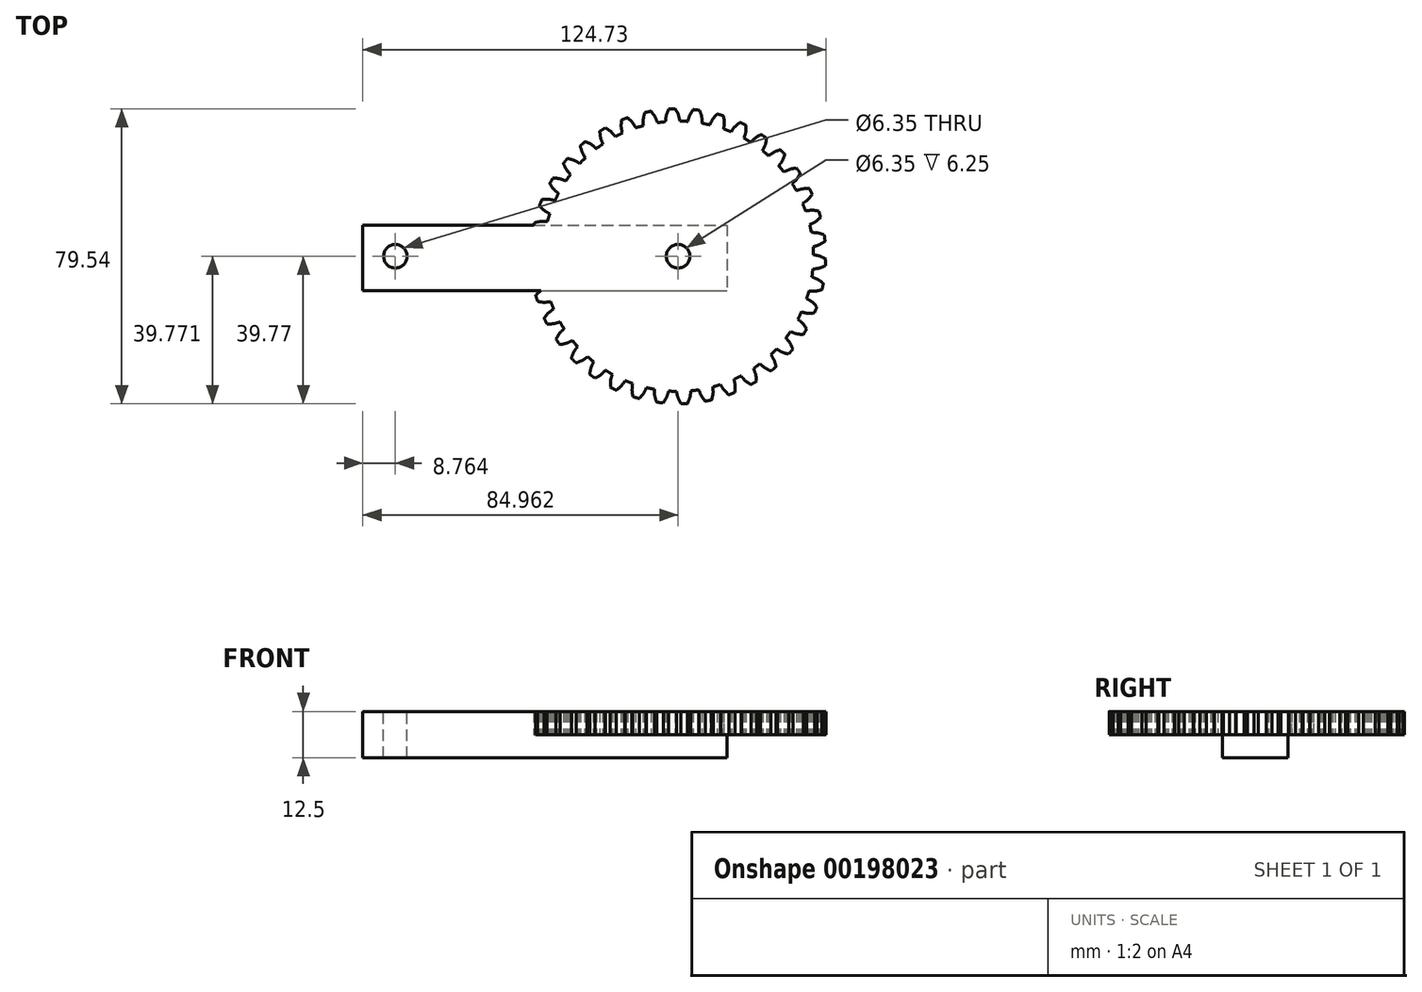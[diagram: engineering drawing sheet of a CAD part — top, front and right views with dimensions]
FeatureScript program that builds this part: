
annotation { "Feature Type Name" : "Feature", "Feature Type Description" : "" }
export const myFeature = defineFeature(function(context is Context, id is Id, definition is map)
    precondition{}
    {
        {
            var Q0;
            Q0=qCreatedBy(makeId("Top.planeOp"),FACE);
            var sketch = newSketch(context, id + "F0", { "sketchPlane" : qUnion([Q0])});
            skCircle(sketch, "E0", {"center": v(0, 0) * mm, "radius": 38.1 * mm, "construction": true});
            skLineSegment(sketch, "E1", {"start": v(0, 0) * mm, "end": v(0, 54.47) * mm, "construction": true});
            skLineSegment(sketch, "E2", {"start": v(-40.8, 38.1) * mm, "end": v(45.04, 38.1) * mm, "construction": true});
            skLineSegment(sketch, "E3", {"start": v(-12.24, 33.64) * mm, "end": v(18.8, 44.94) * mm, "construction": true});
            skLineSegment(sketch, "E4", {"start": v(0, 0) * mm, "end": v(-12.24, 33.64) * mm, "construction": true});
            skCircle(sketch, "E5", {"center": v(0, 0) * mm, "radius": 35.8 * mm, "construction": true});
            skPoint(sketch, "E6", {"position": v(-12.24, 33.64) * mm});
            skPoint(sketch, "E7", {"position": v(0, 38.1) * mm});
            skPoint(sketch, "E8", {"position": v(-16.8, 31.61) * mm});
            skLineSegment(sketch, "E9", {"start": v(-16.8, 31.61) * mm, "end": v(-0.9, 40.1) * mm, "construction": true});
            skArc(sketch, "E10", {"start": v(-7.44, 35.02) * mm, "mid": v(-9.87, 34.42) * mm, "end": v(-12.24, 33.64) * mm});
            skArc(sketch, "E11", {"start": v(-12.24, 33.64) * mm, "mid": v(-14.56, 32.7) * mm, "end": v(-16.8, 31.61) * mm});
            skLineSegment(sketch, "E12", {"start": v(-7.44, 35.02) * mm, "end": v(0.41, 36.69) * mm, "construction": true});
            skLineSegment(sketch, "E13", {"start": v(0, 38.1) * mm, "end": v(0, 0) * mm, "construction": true});
            skLineSegment(sketch, "E14", {"start": v(0.41, 36.69) * mm, "end": v(0.43, 36.44) * mm});
            skArc(sketch, "E15.trimOffspring", {"start": v(0, 36.44) * mm, "mid": v(0, 36.44) * mm, "end": v(0, 36.44) * mm});
            skLineSegment(sketch, "E16", {"start": v(0, 0) * mm, "end": v(-1.9, 46.38) * mm, "construction": true});
            skLineSegment(sketch, "E17.0.MirrorCS", {"start": v(5.36, 0.33) * mm, "end": v(1.52, 46.59) * mm, "construction": true});
            skLineSegment(sketch, "E18.0.MirrorCS", {"start": v(-3.43, 36.53) * mm, "end": v(-3.42, 36.28) * mm});
            skArc(sketch, "E19.converted", {"start": v(-3.42, 36.28) * mm, "mid": v(1.5, -36.41) * mm, "end": v(0.43, 36.44) * mm});
            skLineSegment(sketch, "E20", {"start": v(-3.42, 36.28) * mm, "end": v(-3.42, 36.28) * mm});
            skLineSegment(sketch, "E21", {"start": v(0.43, 36.44) * mm, "end": v(0.43, 36.44) * mm});
            skArc(sketch, "E22.trimOffspring", {"start": v(0.43, 36.44) * mm, "mid": v(-1.5, 36.41) * mm, "end": v(-3.42, 36.28) * mm});
            skArc(sketch, "E23.0", {"start": v(-0.74, 39.77) * mm, "mid": v(-1.64, 39.74) * mm, "end": v(-2.53, 39.7) * mm});
            skFitSpline(sketch, "E24.trimOffspring", {"points": [v(-2.4, 40.03) * mm, v(-3.13, 37.97) * mm, v(-3.43, 36.53) * mm], "startDerivative": vector(-1.5, -3.87) * mm, "endDerivative": vector(-0.5, -3.06) * mm});
            skFitSpline(sketch, "E25.trimOffspring", {"points": [v(-0.9, 40.1) * mm, v(0, 38.1) * mm, v(0.41, 36.69) * mm], "startDerivative": vector(1.82, -3.74) * mm, "endDerivative": vector(0.75, -3.01) * mm});
            skPoint(sketch, "E26.start.orphan", {"position": v(-0.86, 40.02) * mm});
            skPoint(sketch, "E27.trimOffspring.end.orphan", {"position": v(-2.43, 39.95) * mm});
            skCircle(sketch, "E28", {"center": v(0, 0) * mm, "radius": 3.17 * mm});
            skSolve(sketch);
        }
        {
            var Q0;
            Q0=qCreatedBy(makeId("Top.planeOp"),FACE);
            var sketch = newSketch(context, id + "F1", { "sketchPlane" : qUnion([Q0])});
            skFitSpline(sketch, "E29.0", {"points": [v(-2.4, 40.03) * mm, v(-2.68, 39.32) * mm, v(-3.18, 38.02) * mm, v(-3.35, 37) * mm, v(-3.43, 36.53) * mm]});
            skFitSpline(sketch, "E30.0", {"points": [v(-0.9, 40.1) * mm, v(-0.56, 39.4) * mm, v(0.05, 38.15) * mm, v(0.3, 37.14) * mm, v(0.41, 36.69) * mm]});
            skLineSegment(sketch, "E30.1", {"start": v(0.41, 36.69) * mm, "end": v(0.43, 36.44) * mm});
            skLineSegment(sketch, "E30.2", {"start": v(-3.43, 36.53) * mm, "end": v(-3.42, 36.28) * mm});
            skArc(sketch, "E30.3", {"start": v(-0.74, 39.77) * mm, "mid": v(-1.64, 39.74) * mm, "end": v(-2.53, 39.7) * mm});
            skArc(sketch, "E31.0", {"start": v(-3.42, 36.28) * mm, "mid": v(1.5, -36.41) * mm, "end": v(0.43, 36.44) * mm});
            skSolve(sketch);
        }
        {
            var Q0;
            Q0=makeQuery(id+"F1.imprint","IMPRINT",FACE,{"disambiguationData":[TD([[makeQuery(id+"F1.imprint","IMPRINT",EDGE,{"derivedFrom":sQuery(id+"F1.wireOp",EDGE,"E29.0")}),1.0]])]});
            extrude(context, id + "F2", {"entities" : qUnion([Q0]), "depth" : 25 / 4 * mm});
        }
        {
            var Q0;
            Q0=makeQuery(id+"F2.opExtrude","CAP_FACE",FACE,{"disambiguationData":[OSD([sQuery(id+"F1.wireOp",EDGE,"E29.0"),sQuery(id+"F1.wireOp",EDGE,"E30.0"),sQuery(id+"F1.wireOp",EDGE,"E30.1"),sQuery(id+"F1.wireOp",EDGE,"E30.2"),sQuery(id+"F1.wireOp",EDGE,"E30.3"),sQuery(id+"F1.wireOp",EDGE,"E31.0")])],"isStart":false});
            var Q1;
            Q1=makeQuery(id+"F2.opExtrude","SWEPT_BODY",BODY,{"disambiguationData":[OSD([sQuery(id+"F1.wireOp",EDGE,"E29.0"),sQuery(id+"F1.wireOp",EDGE,"E30.0"),sQuery(id+"F1.wireOp",EDGE,"E30.1"),sQuery(id+"F1.wireOp",EDGE,"E30.2"),sQuery(id+"F1.wireOp",EDGE,"E30.3"),sQuery(id+"F1.wireOp",EDGE,"E31.0")])]});
            var Q2;
            Q2=sQuery(id+"F1.wireOp",EDGE,"E31.0");
            circularPattern(context, id + "F3", {"entities" : qUnion([Q1]), "axis" : qUnion([Q2]), "angle" : 360 * degree, "instanceCount" : 38, "equalSpace" : true});
        }
        {
            var Q0;
            Q0=qCreatedBy(makeId("Top.planeOp"),FACE);
            var sketch = newSketch(context, id + "F4", { "sketchPlane" : qUnion([Q0])});
            skCircle(sketch, "E32", {"center": v(0, 0) * mm, "radius": 3.17 * mm});
            skLineSegment(sketch, "E33", {"start": v(-38.1, 43.64) * mm, "end": v(-38.1, -32.57) * mm, "construction": true});
            skCircle(sketch, "E34.0.MirrorC", {"center": v(-76.2, 0) * mm, "radius": 3.17 * mm});
            skLineSegment(sketch, "E35.bottom", {"start": v(-84.96, 8.41) * mm, "end": v(13.2, 8.41) * mm});
            skLineSegment(sketch, "E35.top", {"start": v(-84.96, -9.3) * mm, "end": v(13.2, -9.3) * mm});
            skLineSegment(sketch, "E35.left", {"start": v(-84.96, 8.41) * mm, "end": v(-84.96, -9.3) * mm});
            skLineSegment(sketch, "E35.right", {"start": v(13.2, 8.41) * mm, "end": v(13.2, -9.3) * mm});
            skLineSegment(sketch, "E36", {"start": v(-76.2, 0) * mm, "end": v(0, 0) * mm, "construction": true});
            skSolve(sketch);
        }
        {
            var Q0;
            Q0=makeQuery(id+"F4.imprint","IMPRINT",FACE,{"disambiguationData":[TD([[makeQuery(id+"F4.imprint","IMPRINT",EDGE,{"derivedFrom":sQuery(id+"F4.wireOp",EDGE,"E32")}),-1.0]])]});
            var Q1;
            Q1=makeQuery(id+"F4.imprint","IMPRINT",FACE,{"disambiguationData":[TD([[makeQuery(id+"F4.imprint","IMPRINT",EDGE,{"derivedFrom":sQuery(id+"F4.wireOp",EDGE,"E34.0.MirrorC")}),-1.0]])]});
            var Q2;
            Q2=makeQuery(id+"F4.imprint","IMPRINT",FACE,{"disambiguationData":[TD([[makeQuery(id+"F4.imprint","IMPRINT",EDGE,{"derivedFrom":sQuery(id+"F4.wireOp",EDGE,"E32")}),1.0]])]});
            extrude(context, id + "F5", {"entities" : qUnion([Q0, Q1, Q2]), "oppositeDirection" : true, "depth" : 25 / 4 * mm});
        }
        {
            var Q0;
            Q0=makeQuery(id+"F4.imprint","IMPRINT",FACE,{"disambiguationData":[TD([[makeQuery(id+"F4.imprint","IMPRINT",EDGE,{"derivedFrom":sQuery(id+"F4.wireOp",EDGE,"E34.0.MirrorC")}),-1.0]])]});
            var Q1;
            Q1=makeQuery(id+"F4.imprint","IMPRINT",FACE,{"disambiguationData":[TD([[makeQuery(id+"F4.imprint","IMPRINT",EDGE,{"derivedFrom":sQuery(id+"F4.wireOp",EDGE,"E32")}),1.0]])]});
            extrude(context, id + "F6", {"entities" : qUnion([Q0, Q1]), "operationType" : NewBodyOperationType.ADD, "depth" : 25 / 4 * mm});
        }
        {
            var Q0;
            Q0=makeQuery(id+"F0.imprint","IMPRINT",FACE,{"disambiguationData":[TD([[makeQuery(id+"F0.imprint","IMPRINT",EDGE,{"derivedFrom":sQuery(id+"F0.wireOp",EDGE,"E28")}),1.0]])]});
            extrude(context, id + "F7", {"entities" : qUnion([Q0]), "operationType" : NewBodyOperationType.REMOVE, "depth" : 25 * mm});
        }
    });
